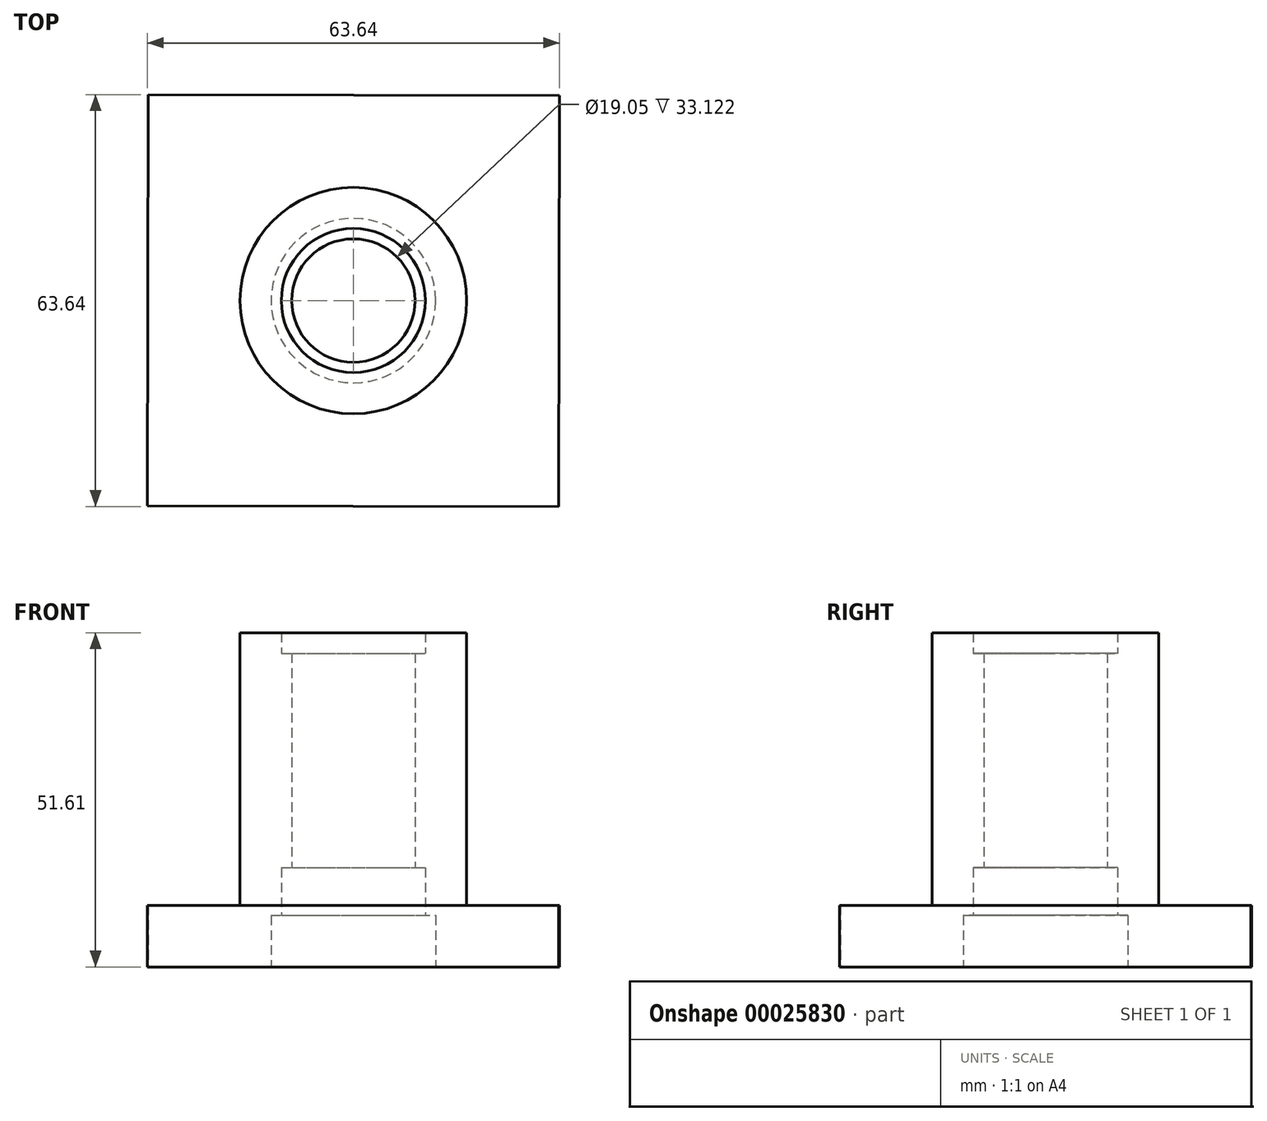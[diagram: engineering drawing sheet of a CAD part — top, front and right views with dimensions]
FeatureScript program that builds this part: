
annotation { "Feature Type Name" : "Feature", "Feature Type Description" : "" }
export const myFeature = defineFeature(function(context is Context, id is Id, definition is map)
    precondition{}
    {
        {
            var Q0;
            Q0=qCreatedBy(makeId("Front.planeOp"),FACE);
            var sketch = newSketch(context, id + "F0", { "sketchPlane" : qUnion([Q0])});
            skLineSegment(sketch, "E0", {"start": v(-63.9, 0) * mm, "end": v(0, 0) * mm, "construction": true});
            skLineSegment(sketch, "E1", {"start": v(0, 0) * mm, "end": v(0, 72.66) * mm, "construction": true});
            skLineSegment(sketch, "E2", {"start": v(-31.75, 9.53) * mm, "end": v(-31.75, 0) * mm});
            skLineSegment(sketch, "E3", {"start": v(-31.75, 0) * mm, "end": v(-12.7, 0) * mm});
            skLineSegment(sketch, "E4", {"start": v(-12.7, 0) * mm, "end": v(-12.7, 7.95) * mm});
            skLineSegment(sketch, "E5", {"start": v(-12.7, 7.95) * mm, "end": v(-11.13, 7.95) * mm});
            skLineSegment(sketch, "E6", {"start": v(-11.13, 7.95) * mm, "end": v(-11.13, 15.32) * mm});
            skLineSegment(sketch, "E7", {"start": v(-11.13, 15.32) * mm, "end": v(-9.52, 15.32) * mm});
            skLineSegment(sketch, "E8", {"start": v(-9.52, 15.32) * mm, "end": v(-9.53, 48.44) * mm});
            skLineSegment(sketch, "E9", {"start": v(-9.53, 48.44) * mm, "end": v(-11.13, 48.44) * mm});
            skLineSegment(sketch, "E10", {"start": v(-11.13, 48.44) * mm, "end": v(-11.13, 51.61) * mm});
            skLineSegment(sketch, "E11", {"start": v(-11.13, 51.61) * mm, "end": v(-17.49, 51.61) * mm});
            skLineSegment(sketch, "E12", {"start": v(-17.49, 51.61) * mm, "end": v(-17.49, 9.53) * mm});
            skLineSegment(sketch, "E13", {"start": v(-31.75, 9.53) * mm, "end": v(-17.49, 9.53) * mm});
            skSolve(sketch);
        }
        {
            var Q0;
            Q0=makeQuery(id+"F0.imprint","IMPRINT",FACE,{"disambiguationData":[TD([[makeQuery(id+"F0.imprint","IMPRINT",EDGE,{"derivedFrom":sQuery(id+"F0.wireOp",EDGE,"E2")}),1.0]])]});
            var Q1;
            Q1=sQuery(id+"F0.wireOp",EDGE,"E1");
            revolve(context, id + "F1", {"entities" : qUnion([Q0]), "axis" : qUnion([Q1]), "revolveType" : RevolveType.FULL});
        }
        {
            var Q0;
            Q0=makeQuery(id+"F1.opRevolve","SWEPT_FACE",FACE,{"disambiguationData":[OSD([sQuery(id+"F0.wireOp",EDGE,"E3")])]});
            var sketch = newSketch(context, id + "F2", { "sketchPlane" : qUnion([Q0])});
            skCircle(sketch, "E14.cCircle", {"center": v(0, 0) * mm, "radius": 31.75 * mm, "construction": true});
            skLineSegment(sketch, "E15.0", {"start": v(31.82, -31.68) * mm, "end": v(-31.68, -31.82) * mm});
            skLineSegment(sketch, "E15.1", {"start": v(-31.68, -31.82) * mm, "end": v(-31.82, 31.68) * mm});
            skLineSegment(sketch, "E15.2", {"start": v(-31.82, 31.68) * mm, "end": v(31.68, 31.82) * mm});
            skLineSegment(sketch, "E15.3", {"start": v(31.68, 31.82) * mm, "end": v(31.82, -31.68) * mm});
            skPoint(sketch, "E15.0.midPoint", {"position": v(0.07, -31.75) * mm});
            skLineSegment(sketch, "E16", {"start": v(0, 0) * mm, "end": v(0, 47.05) * mm, "construction": true});
            skLineSegment(sketch, "E17", {"start": v(0, 0) * mm, "end": v(-49.58, 0) * mm, "construction": true});
            skLineSegment(sketch, "E18", {"start": v(0, 31.75) * mm, "end": v(-50.29, 31.75) * mm, "construction": true});
            skSolve(sketch);
        }
        {
            var Q0;
            {var subQ1=sQuery(id+"F2.wireOp",EDGE,"E15.3");var subQ3=sQuery(id+"F2.wireOp",EDGE,"E15.0");var subQ5=makeQuery(id+"F2.imprint","INTERSECT",VERTEX,{"derivedFrom":[subQ3,subQ1]});Q0=makeQuery(id+"F2.imprint","IMPRINT",FACE,{"disambiguationData":[TD([[makeQuery(id+"F2.imprint","IMPRINT",EDGE,{"disambiguationData":[TD([[subQ5,-1.0]])],"derivedFrom":subQ3}),-1.0]])]});}
            var Q1;
            {var subQ1=sQuery(id+"F2.wireOp",EDGE,"E15.1");var subQ3=sQuery(id+"F2.wireOp",EDGE,"E15.0");var subQ5=makeQuery(id+"F2.imprint","INTERSECT",VERTEX,{"derivedFrom":[subQ3,subQ1]});Q1=makeQuery(id+"F2.imprint","IMPRINT",FACE,{"disambiguationData":[TD([[makeQuery(id+"F2.imprint","IMPRINT",EDGE,{"disambiguationData":[TD([[subQ5,1.0]])],"derivedFrom":subQ3}),-1.0]])]});}
            var Q2;
            {var subQ1=sQuery(id+"F2.wireOp",EDGE,"E15.2");var subQ3=sQuery(id+"F2.wireOp",EDGE,"E15.1");var subQ5=makeQuery(id+"F2.imprint","INTERSECT",VERTEX,{"derivedFrom":[subQ3,subQ1]});Q2=makeQuery(id+"F2.imprint","IMPRINT",FACE,{"disambiguationData":[TD([[makeQuery(id+"F2.imprint","IMPRINT",EDGE,{"disambiguationData":[TD([[subQ5,1.0]])],"derivedFrom":subQ3}),-1.0]])]});}
            var Q3;
            {var subQ1=sQuery(id+"F2.wireOp",EDGE,"E15.3");var subQ3=sQuery(id+"F2.wireOp",EDGE,"E15.2");var subQ5=makeQuery(id+"F2.imprint","INTERSECT",VERTEX,{"derivedFrom":[subQ3,subQ1]});Q3=makeQuery(id+"F2.imprint","IMPRINT",FACE,{"disambiguationData":[TD([[makeQuery(id+"F2.imprint","IMPRINT",EDGE,{"disambiguationData":[TD([[subQ5,1.0]])],"derivedFrom":subQ3}),-1.0]])]});}
            extrude(context, id + "F3", {"entities" : qUnion([Q0, Q1, Q2, Q3]), "operationType" : NewBodyOperationType.ADD, "oppositeDirection" : true, "depth" : 9.52 * mm});
        }
    });
